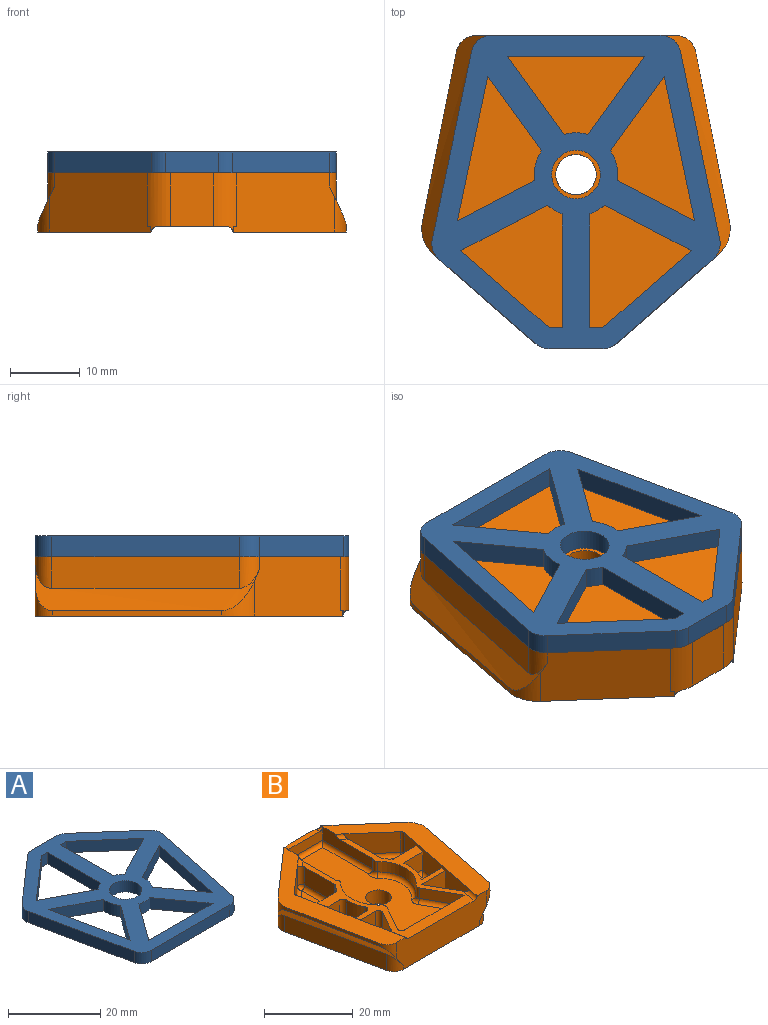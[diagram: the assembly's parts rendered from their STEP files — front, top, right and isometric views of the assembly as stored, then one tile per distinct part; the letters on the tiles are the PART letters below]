
ASSEMBLY  parts=2 mates=1
PART A: 37 faces, bbox 41.4x45x3 mm
  f0: plane 45x41.41mm, normal (0,0,1), area 760mm2, adj f2,f3,f4,f5,f6,f7,f8,f9
  f1: plane 45x41.41mm, normal (0,0,-1), area 760mm2, adj f2,f3,f4,f5,f6,f7,f8,f9
  f2: plane 26.9x5.64mm, normal (-0.98,-0.21,0), area 82.4mm2, adj f0,f1,f34,f36
  f3: plane 24.13x3mm, normal (0,-1,0), area 72.4mm2, adj f0,f1,f33,f34
  f4: plane 7.75x3mm, normal (0,1,0), area 23.2mm2, adj f0,f1,f31,f35
  f5: plane 13.83x12.1mm, normal (-0.66,0.75,0), area 55.1mm2, adj f0,f1,f35,f36
  f6: plane 26.9x5.64mm, normal (0.98,-0.21,0), area 82.4mm2, adj f0,f1,f32,f33
  f7: plane 13.83x12.1mm, normal (0.66,0.75,0), area 55.1mm2, adj f0,f1,f31,f32
  f8: cylinder r=3.5mm len=7mm, axis (0,0,1), area 66mm2, adj f0,f1
  f9: plane 10.67x7.74mm, normal (0.81,0.59,0), area 39.5mm2, adj f0,f1,f10,f12
  f10: plane 20.74x4.35mm, normal (-0.98,0.21,0), area 63.6mm2, adj f0,f1,f9,f11
  f11: plane 11.09x5.81mm, normal (0.46,-0.89,0), area 37.5mm2, adj f0,f1,f10,f12
  f12: cylinder r=6mm len=4.26mm, axis (0,0,1), area 13.4mm2, adj f0,f1,f9,f11
  f13: plane 12.66x11.08mm, normal (0.66,-0.75,0), area 50.5mm2, adj f0,f1,f14,f17
  f14: plane 12.45x6.52mm, normal (0.46,0.89,0), area 42.2mm2, adj f0,f1,f13,f15
  f15: cylinder r=6mm len=3mm, axis (0,0,1), area 7.4mm2, adj f0,f1,f14,f16
  f16: plane 16.34x3mm, normal (-1,0,0), area 49mm2, adj f0,f1,f15,f17
  f17: plane 3x1.87mm, normal (0,-1,0), area 5.6mm2, adj f0,f1,f13,f16
  f18: plane 20.74x4.35mm, normal (0.98,0.21,0), area 63.6mm2, adj f0,f1,f19,f21
  f19: plane 10.67x7.74mm, normal (-0.81,0.59,0), area 39.5mm2, adj f0,f1,f18,f20
  f20: cylinder r=6mm len=4.26mm, axis (0,0,1), area 13.4mm2, adj f0,f1,f19,f21
  f21: plane 11.09x5.81mm, normal (-0.46,-0.89,0), area 37.5mm2, adj f0,f1,f18,f20
  f22: cylinder r=6mm len=3.4mm, axis (0,0,1), area 10.3mm2, adj f0,f1,f23,f25
  f23: plane 11.25x8.15mm, normal (0.81,-0.59,0), area 41.7mm2, adj f0,f1,f22,f24
  f24: plane 19.71x3mm, normal (0,1,0), area 59.1mm2, adj f0,f1,f23,f25
  f25: plane 11.25x8.15mm, normal (-0.81,-0.59,0), area 41.7mm2, adj f0,f1,f22,f24
  f26: plane 12.45x6.52mm, normal (-0.46,0.89,0), area 42.2mm2, adj f0,f1,f27,f30
  f27: plane 12.66x11.08mm, normal (-0.66,-0.75,0), area 50.5mm2, adj f0,f1,f26,f28
  f28: plane 3x1.87mm, normal (0,-1,0), area 5.6mm2, adj f0,f1,f27,f29
  f29: plane 16.34x3mm, normal (1,0,0), area 49mm2, adj f0,f1,f28,f30
  f30: cylinder r=6mm len=3mm, axis (0,0,1), area 7.4mm2, adj f0,f1,f26,f29
  f31: cylinder r=3mm len=3mm, axis (0,0,-1), area 6.5mm2, adj f0,f1,f4,f7
  f32: cylinder r=3mm len=3mm, axis (0,0,-1), area 9.5mm2, adj f0,f1,f6,f7
  f33: cylinder r=3mm len=3mm, axis (0,0,1), area 12.3mm2, adj f0,f1,f3,f6
  f34: cylinder r=3mm len=3mm, axis (0,0,1), area 12.3mm2, adj f0,f1,f2,f3
  f35: cylinder r=3mm len=3mm, axis (0,0,-1), area 6.5mm2, adj f0,f1,f4,f5
  f36: cylinder r=3mm len=3mm, axis (0,0,-1), area 9.5mm2, adj f0,f1,f2,f5
PART B: 149 faces, bbox 45.3x45.2x8.6 mm
  f0: plane 15.91x3.7mm, normal (-1,0,0), area 49.7mm2, adj f3,f7,f18,f86,f98,f138
  f1: plane 14.91x3.7mm, normal (1,0,0), area 46mm2, adj f6,f14,f18,f89,f99,f135
  f2: plane 19.09x2.9mm, normal (0,1,0), area 55.3mm2, adj f9,f15,f18,f148
  f3: plane 10.82x3.7mm, normal (0,-1,0), area 31.6mm2, adj f0,f14,f19,f97,f136
  f4: plane 7.71x4.36mm, normal (0.87,-0.49,0), area 25.7mm2, adj f13,f15,f18,f144
  f5: cylinder r=8.5mm len=12.7mm, axis (0,0,1), area 41.6mm2, adj f12,f13,f18,f140
  f6: plane 2.9x0.2mm, normal (0.79,0.61,0), area 0.7mm2, adj f1,f12,f18,f134
  f7: plane 2.9x0.2mm, normal (-0.79,0.61,0), area 0.7mm2, adj f0,f11,f18,f139
  f8: cylinder r=8.5mm len=12.7mm, axis (0,0,1), area 41.6mm2, adj f10,f11,f18,f143
  f9: plane 9.2x5.2mm, normal (-0.87,-0.49,0), area 30.6mm2, adj f2,f10,f18,f147
  f10: cylinder r=1mm len=2.9mm, axis (0,0,1), area 4mm2, adj f8,f9,f18,f145
  f11: cylinder r=1mm len=2.9mm, axis (0,0,1), area 4.2mm2, adj f7,f8,f18,f141
  f12: cylinder r=1mm len=2.9mm, axis (0,0,1), area 4.2mm2, adj f5,f6,f18,f137
  f13: cylinder r=1mm len=2.9mm, axis (0,0,1), area 4mm2, adj f4,f5,f18,f142
  f14: cylinder r=1mm len=3.7mm, axis (0,0,1), area 5.1mm2, adj f1,f3,f19,f94,f133
  f15: cylinder r=1mm len=2.9mm, axis (0,0,1), area 6mm2, adj f2,f4,f18,f146
  f16: plane 5.7x3.83mm, normal (0.98,0.2,0), area 22.3mm2, adj f82,f89,f103,f111
  f17: plane 5.7x5.38mm, normal (0.98,0.2,0), area 31.3mm2, adj f75,f89,f101,f116
  f18: plane 38.19x31.53mm, normal (0,0,1), area 218.5mm2, adj f0,f1,f2,f4,f5,f6,f7,f8
  f19: plane 9.86x1.4mm, normal (0,0,1), area 13.4mm2, adj f3,f14,f22,f58,f59,f94,f97
  f20: plane 26.9x5.64mm, normal (-0.98,-0.21,0), area 123.7mm2, adj f24,f25,f128,f130
  f21: plane 28.56x8.56mm, normal (0,-1,0), area 213.2mm2, adj f18,f24,f25,f28,f86,f89,f92,f93
  f22: plane 7.7x6.24mm, normal (0,1,0), area 48.1mm2, adj f19,f24,f58,f59
  f23: plane 14.53x12.71mm, normal (-0.66,0.75,0), area 156.3mm2, adj f24,f25,f30,f59,f88,f89,f91,f130
  f24: plane 45x41.41mm, normal (0,0,-1), area 1433.9mm2, adj f20,f21,f22,f23,f26,f27,f29,f58
  f25: bspline ~32.56x10.55mm, area 115.2mm2, adj f20,f21,f23,f87,f91,f93,f128,f130
  f26: plane 26.9x5.64mm, normal (0.98,-0.21,0), area 123.7mm2, adj f24,f28,f129,f131
  f27: plane 14.53x12.71mm, normal (0.66,0.75,0), area 156.3mm2, adj f24,f28,f31,f58,f85,f86,f90,f131
  f28: bspline ~32.56x10.55mm, area 115.2mm2, adj f21,f26,f27,f84,f90,f92,f129,f131
  f29: cylinder r=2.9mm len=5.8mm, axis (0,0,1), area 69.2mm2, adj f24,f132
  f30: plane 0.8x0.05mm, normal (1,0,0), area 0mm2, adj f23,f59,f88,f89
  f31: plane 0.8x0.05mm, normal (-1,0,0), area 0mm2, adj f27,f58,f85,f86
  f32: plane 7.9x6.91mm, normal (0.66,-0.75,0), area 59.8mm2, adj f83,f89,f109,f111
  f33: plane 9.33x4.9mm, normal (-1,0,0), area 45.7mm2, adj f18,f81,f107,f109
  f34: cylinder r=9.7mm len=4.9mm, axis (0,0,1), area 7.6mm2, adj f18,f79,f105,f107
  f35: plane 6.16x4.92mm, normal (0,1,0), area 30.2mm2, adj f18,f80,f102,f103,f105
  f36: plane 10.74x7.9mm, normal (0,0,1), area 55.4mm2, adj f79,f80,f81,f82,f83
  f37: plane 7.48x4.9mm, normal (0,-1,0), area 36.7mm2, adj f18,f38,f54,f60
  f38: plane 9.78x5.7mm, normal (0.87,0.49,0), area 55.4mm2, adj f18,f37,f54,f61,f96
  f39: plane 5.95x4.55mm, normal (0,0,1), area 13.5mm2, adj f60,f61,f62
  f40: cylinder r=9.7mm len=7.38mm, axis (0,0,1), area 38.3mm2, adj f18,f41,f42,f64
  f41: plane 6.14x4.9mm, normal (0,-1,0), area 30.1mm2, adj f18,f40,f54,f66
  f42: plane 6.48x4.9mm, normal (0,1,0), area 31.7mm2, adj f18,f40,f54,f63
  f43: plane 5.38x4.94mm, normal (0,0,1), area 19.3mm2, adj f63,f64,f65,f66
  f44: plane 4.9x3.81mm, normal (0,-1,0), area 18.7mm2, adj f18,f77,f101,f120
  f45: cylinder r=9.7mm len=4.9mm, axis (0,0,1), area 24.7mm2, adj f18,f78,f118,f120
  f46: plane 4.92x3.87mm, normal (0,1,0), area 18.9mm2, adj f18,f76,f115,f116,f118
  f47: plane 5.38x4.94mm, normal (0,0,1), area 19.3mm2, adj f75,f76,f77,f78
  f48: plane 5.95x5.7mm, normal (0.98,0.2,0), area 34.6mm2, adj f73,f89,f114,f122
  f49: plane 4.9x4.55mm, normal (0,-1,0), area 22.3mm2, adj f18,f74,f114,f124
  f50: plane 5.95x4.9mm, normal (-0.87,0.49,0), area 33.5mm2, adj f18,f72,f122,f124
  f51: plane 5.95x4.55mm, normal (0,0,1), area 13.5mm2, adj f72,f73,f74
  f52: plane 11.9x5.7mm, normal (1,0,0), area 58.5mm2, adj f18,f53,f56,f69,f98
  f53: plane 9.55x8.36mm, normal (-0.66,-0.75,0), area 72.4mm2, adj f52,f71,f86,f126
  f54: plane 25.96x5.7mm, normal (-0.98,0.2,0), area 130.1mm2, adj f18,f37,f38,f41,f42,f55,f62,f65
  f55: plane 7.58x4.9mm, normal (0,1,0), area 37.1mm2, adj f18,f54,f56,f68
  f56: cylinder r=9.7mm len=4.9mm, axis (0,0,1), area 12.1mm2, adj f18,f52,f55,f67
  f57: plane 10.74x7.9mm, normal (0,0,1), area 55.4mm2, adj f67,f68,f69,f70,f71
  f58: cylinder r=5mm len=8.5mm, axis (0,0,-1), area 27.9mm2, adj f19,f22,f24,f27,f31,f85,f97
  f59: cylinder r=5mm len=8.5mm, axis (0,0,-1), area 27.9mm2, adj f19,f22,f23,f24,f30,f88,f94
  f60: cylinder r=1mm len=7.48mm, axis (1,0,0), area 10.1mm2, adj f37,f39,f61,f62
  f61: cylinder r=1mm len=10.27mm, axis (-0.49,0.87,0), area 15.1mm2, adj f38,f39,f60,f62
  f62: cylinder r=1mm len=9.98mm, axis (-0.2,-0.98,0), area 13.4mm2, adj f39,f54,f60,f61
  f63: cylinder r=1mm len=6.48mm, axis (-1,0,0), area 8.6mm2, adj f42,f43,f64,f65
  f64: torus R=10.7mm, axis (0,0,-1), area 11mm2, adj f40,f43,f63,f66
  f65: cylinder r=1mm len=7.58mm, axis (-0.2,-0.98,0), area 10.7mm2, adj f43,f54,f63,f66
  f66: cylinder r=1mm len=6.14mm, axis (1,0,0), area 8.3mm2, adj f41,f43,f64,f65
  f67: torus R=10.7mm, axis (0,0,-1), area 3.4mm2, adj f56,f57,f68,f69
  f68: cylinder r=1mm len=7.58mm, axis (-1,0,0), area 11.1mm2, adj f55,f57,f67,f70
  f69: cylinder r=1mm len=11.9mm, axis (0,1,0), area 17.1mm2, adj f52,f57,f67,f71
  f70: cylinder r=1mm len=4.83mm, axis (-0.2,-0.98,0), area 7mm2, adj f54,f57,f68,f127
  f71: cylinder r=1mm len=10.21mm, axis (0.75,-0.66,0), area 18.7mm2, adj f53,f57,f69,f127
  f72: cylinder r=1mm len=6.44mm, axis (-0.49,-0.87,0), area 10.7mm2, adj f50,f51,f123,f125
  f73: cylinder r=1mm len=6.14mm, axis (-0.2,0.98,0), area 9.5mm2, adj f48,f51,f113,f123
  f74: cylinder r=1mm len=4.55mm, axis (1,0,0), area 7.1mm2, adj f49,f51,f113,f125
  f75: cylinder r=1mm len=5.58mm, axis (-0.2,0.98,0), area 8.6mm2, adj f17,f47,f100,f117
  f76: cylinder r=1mm len=3.87mm, axis (-1,0,0), area 6.1mm2, adj f46,f47,f117,f119
  f77: cylinder r=1mm len=3.81mm, axis (1,0,0), area 6mm2, adj f44,f47,f100,f121
  f78: torus R=10.7mm, axis (0,0,-1), area 8.2mm2, adj f45,f47,f119,f121
  f79: torus R=10.7mm, axis (0,0,-1), area 2.5mm2, adj f34,f36,f106,f108
  f80: cylinder r=1mm len=6.16mm, axis (-1,0,0), area 9.7mm2, adj f35,f36,f104,f106
  f81: cylinder r=1mm len=9.33mm, axis (0,-1,0), area 14.7mm2, adj f33,f36,f108,f110
  f82: cylinder r=1mm len=4.03mm, axis (-0.2,0.98,0), area 6.1mm2, adj f16,f36,f104,f112
  f83: cylinder r=1mm len=8.55mm, axis (0.75,0.66,0), area 16.5mm2, adj f32,f36,f110,f112
  f84: plane 24.34x4.86mm, normal (0.98,-0.2,0), area 19.9mm2, adj f28,f86,f90,f92
  f85: plane 0.5x0.44mm, normal (0,0,-1), area 0mm2, adj f27,f31,f58
  f86: plane 44.2x16.23mm, normal (0,0,1), area 220.4mm2, adj f0,f21,f27,f31,f53,f54,f84,f90
  f87: plane 24.34x4.86mm, normal (-0.98,-0.2,0), area 19.9mm2, adj f25,f89,f91,f93
  f88: plane 0.5x0.44mm, normal (0,0,-1), area 0mm2, adj f23,f30,f59
  f89: plane 44.2x16.23mm, normal (0,0,1), area 220.4mm2, adj f1,f16,f17,f21,f23,f30,f32,f48
  f90: cylinder r=5mm len=5.11mm, axis (0,0,-1), area 12mm2, adj f27,f28,f84,f86
  f91: cylinder r=5mm len=5.11mm, axis (0,0,1), area 12mm2, adj f23,f25,f87,f89
  f92: cylinder r=3mm len=4.36mm, axis (0,0,1), area 8.5mm2, adj f21,f28,f84,f86
  f93: cylinder r=3mm len=4.36mm, axis (0,0,-1), area 8.5mm2, adj f21,f25,f87,f89
  f94: cylinder r=1mm len=2.06mm, axis (0,-1,0), area 1.5mm2, adj f14,f19,f59,f89
  f95: cylinder r=1mm len=6.02mm, axis (0.2,-0.98,0), area 7.1mm2, adj f18,f21,f89,f122
  f96: cylinder r=1mm len=4.5mm, axis (-0.2,-0.98,0), area 5mm2, adj f18,f21,f38,f86
  f97: cylinder r=1mm len=1.06mm, axis (0,-1,0), area 1.1mm2, adj f3,f19,f58,f86
  f98: cylinder r=1mm len=2.69mm, axis (0.75,-0.66,0), area 2.5mm2, adj f0,f18,f52,f86
  f99: cylinder r=1mm len=3.7mm, axis (-0.75,-0.66,0), area 4.1mm2, adj f1,f18,f89,f109
  f100: sphere r=1mm, area 1.8mm2, adj f75,f77,f101
  f101: cylinder r=1mm len=5.7mm, axis (0,0,-1), area 9.2mm2, adj f17,f18,f44,f100,f102
  f102: cylinder r=1mm len=4.95mm, axis (0.2,-0.98,0), area 4.8mm2, adj f18,f35,f89,f101,f103
  f103: cylinder r=1mm len=5.7mm, axis (0,0,1), area 7.3mm2, adj f16,f35,f102,f104
  f104: sphere r=1mm, area 1.4mm2, adj f80,f82,f103
  f105: cylinder r=1mm len=4.9mm, axis (0,0,1), area 5.1mm2, adj f18,f34,f35,f106
  f106: sphere r=1mm, area 1mm2, adj f79,f80,f105
  f107: cylinder r=1mm len=4.9mm, axis (0,0,1), area 3.3mm2, adj f18,f33,f34,f108
  f108: sphere r=1mm, area 0.7mm2, adj f79,f81,f107
  f109: cylinder r=1mm len=5.7mm, axis (0,0,1), area 11.7mm2, adj f18,f32,f33,f99,f110
  f110: sphere r=1mm, area 2.3mm2, adj f81,f83,f109
  f111: cylinder r=1mm len=5.7mm, axis (0,0,-1), area 6mm2, adj f16,f32,f89,f112
  f112: sphere r=1mm, area 1mm2, adj f82,f83,f111
  f113: sphere r=1mm, area 1.8mm2, adj f73,f74,f114
  f114: cylinder r=1mm len=5.7mm, axis (0,0,-1), area 9.2mm2, adj f18,f48,f49,f113,f115
  f115: cylinder r=1mm len=3.59mm, axis (0.2,-0.98,0), area 2.9mm2, adj f18,f46,f89,f114,f116
  f116: cylinder r=1mm len=5.7mm, axis (0,0,1), area 7.3mm2, adj f17,f46,f115,f117
  f117: sphere r=1mm, area 1.4mm2, adj f75,f76,f116
  f118: cylinder r=1mm len=4.9mm, axis (0,0,1), area 10mm2, adj f18,f45,f46,f119
  f119: sphere r=1mm, area 2mm2, adj f76,f78,f118
  f120: cylinder r=1mm len=4.9mm, axis (0,0,1), area 8mm2, adj f18,f44,f45,f121
  f121: sphere r=1mm, area 1.6mm2, adj f77,f78,f120
  f122: cylinder r=1mm len=5.7mm, axis (0,0,-1), area 12.4mm2, adj f18,f48,f50,f95,f123
  f123: sphere r=1mm, area 2.4mm2, adj f72,f73,f122
  f124: cylinder r=1mm len=4.9mm, axis (0,0,-1), area 10.2mm2, adj f18,f49,f50,f125
  f125: sphere r=1mm, area 2.1mm2, adj f72,f74,f124
  f126: cylinder r=1mm len=5.7mm, axis (0,0,-1), area 6mm2, adj f53,f54,f86,f127
  f127: sphere r=1mm, area 1mm2, adj f70,f71,f126
  f128: cylinder r=3mm len=4.5mm, axis (0,0,-1), area 13.3mm2, adj f20,f21,f24,f25
  f129: cylinder r=3mm len=4.5mm, axis (0,0,1), area 13.3mm2, adj f21,f24,f26,f28
  f130: cylinder r=3mm len=4.5mm, axis (0,0,-1), area 11.4mm2, adj f20,f23,f24,f25
  f131: cylinder r=3mm len=4.5mm, axis (0,0,1), area 11.4mm2, adj f24,f26,f27,f28
  f132: plane 38.6x17.37mm, normal (0,0,1), area 413.5mm2, adj f29,f135,f136,f137,f138,f140,f141,f142
  f133: sphere r=1mm, area 1.6mm2, adj f14,f135,f136
  f134: cylinder r=1mm len=0.97mm, axis (-0.61,0.79,0), area 0.2mm2, adj f6,f135,f137
  f135: cylinder r=1mm len=14.91mm, axis (0,1,0), area 23.2mm2, adj f1,f132,f133,f134,f137
  f136: cylinder r=1mm len=10.82mm, axis (1,0,0), area 16.4mm2, adj f3,f132,f133,f138
  f137: torus R=2mm, axis (0,0,-1), area 3.1mm2, adj f12,f132,f134,f135,f140
  f138: cylinder r=1mm len=15.91mm, axis (0,-1,0), area 24.2mm2, adj f0,f132,f136,f139,f141
  f139: cylinder r=1mm len=0.97mm, axis (0.61,0.79,0), area 0.2mm2, adj f7,f138,f141
  f140: torus R=7.5mm, axis (0,0,-1), area 21.6mm2, adj f5,f132,f137,f142
  f141: torus R=2mm, axis (0,0,-1), area 3.1mm2, adj f11,f132,f138,f139,f143
  f142: torus R=2mm, axis (0,0,-1), area 3mm2, adj f13,f132,f140,f144
  f143: torus R=7.5mm, axis (0,0,-1), area 21.6mm2, adj f8,f132,f141,f145
  f144: cylinder r=1mm len=8.2mm, axis (0.49,0.87,0), area 13.9mm2, adj f4,f132,f142,f146
  f145: torus R=2mm, axis (0,0,-1), area 3mm2, adj f10,f132,f143,f147
  f146: sphere r=1mm, area 2.1mm2, adj f15,f144,f148
  f147: cylinder r=1mm len=9.69mm, axis (0.49,-0.87,0), area 15.6mm2, adj f9,f132,f145,f148
  f148: cylinder r=1mm len=19.09mm, axis (-1,0,0), area 29mm2, adj f2,f132,f146,f147
PLACE A rot(axis=(0,0,-1),180deg) t=(-3.61,-16.86,20.91)mm
PLACE B rot(axis=(1,0,0),180deg) t=(-3.61,-16.86,20.91)mm fixed
MATE slider B.f5 <-> A.f30  axis (0,0,1) through (-3.61,-36.86,20.91)mm
